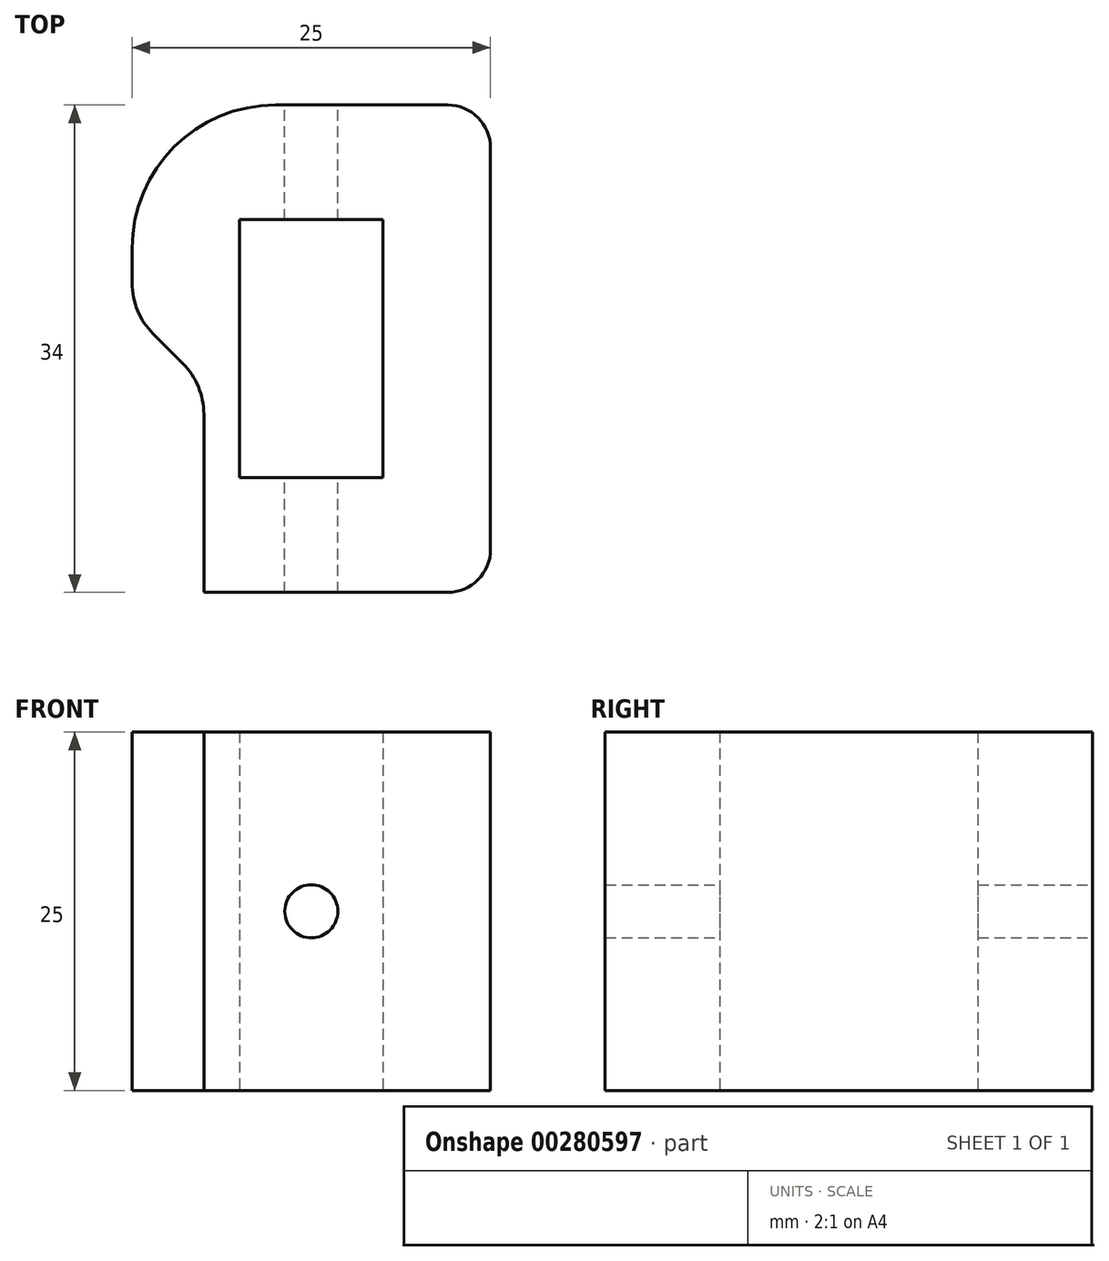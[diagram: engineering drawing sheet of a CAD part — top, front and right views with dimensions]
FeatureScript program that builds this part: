
annotation { "Feature Type Name" : "Feature", "Feature Type Description" : "" }
export const myFeature = defineFeature(function(context is Context, id is Id, definition is map)
    precondition{}
    {
        {
            var Q0;
            Q0=qCreatedBy(makeId("Top.planeOp"),FACE);
            var sketch = newSketch(context, id + "F0", { "sketchPlane" : qUnion([Q0])});
            skLineSegment(sketch, "E0", {"start": v(0, 0) * mm, "end": v(7.5, 0) * mm});
            skLineSegment(sketch, "E1", {"start": v(12.5, 34) * mm, "end": v(12.5, 19.5) * mm});
            skLineSegment(sketch, "E2", {"start": v(12.5, 34) * mm, "end": v(0, 34) * mm});
            skLineSegment(sketch, "E3.MirrorCS", {"start": v(-7.5, 14.5) * mm, "end": v(-12.5, 14.5) * mm, "construction": true});
            skLineSegment(sketch, "E4.MirrorCS", {"start": v(-12.5, 14.5) * mm, "end": v(-12.5, 19.5) * mm, "construction": true});
            skLineSegment(sketch, "E5.MirrorCS", {"start": v(-12.5, 34) * mm, "end": v(-12.5, 19.5) * mm});
            skLineSegment(sketch, "E6.MirrorCS", {"start": v(0, 0) * mm, "end": v(-7.5, 0) * mm});
            skLineSegment(sketch, "E7.MirrorCS", {"start": v(-7.5, 0) * mm, "end": v(-7.5, 14.5) * mm});
            skLineSegment(sketch, "E8.MirrorCS", {"start": v(-12.5, 34) * mm, "end": v(0, 34) * mm});
            skLineSegment(sketch, "E9.MirrorCS", {"start": v(-7.5, 14.5) * mm, "end": v(-12.5, 19.5) * mm});
            skLineSegment(sketch, "E10.0", {"start": v(-10, 21.5) * mm, "end": v(-10, 20.54) * mm});
            skLineSegment(sketch, "E10.2", {"start": v(0, 31.5) * mm, "end": v(0, 31.5) * mm});
            skLineSegment(sketch, "E10.3", {"start": v(-5, 8) * mm, "end": v(-5, 26) * mm});
            skLineSegment(sketch, "E10.6", {"start": v(0, 31.5) * mm, "end": v(0, 31.5) * mm});
            skLineSegment(sketch, "E10.7", {"start": v(10, 21.5) * mm, "end": v(10, 20.54) * mm});
            skLineSegment(sketch, "E10.9", {"start": v(5, 8) * mm, "end": v(5, 26) * mm});
            skLineSegment(sketch, "E11", {"start": v(-5, 8) * mm, "end": v(5, 8) * mm});
            skPoint(sketch, "E12.orphan", {"position": v(-5, -10) * mm});
            skPoint(sketch, "E13.orphan", {"position": v(5, -10) * mm});
            skPoint(sketch, "E14.visualSharp", {"position": v(-10, 31.5) * mm});
            skPoint(sketch, "E15.visualSharp", {"position": v(10, 31.5) * mm});
            skLineSegment(sketch, "E16", {"start": v(12.5, 19.5) * mm, "end": v(12.5, 0) * mm});
            skLineSegment(sketch, "E17", {"start": v(12.5, 0) * mm, "end": v(7.5, 0) * mm});
            skLineSegment(sketch, "E18", {"start": v(-5, 26) * mm, "end": v(5, 26) * mm});
            skSolve(sketch);
        }
        {
            var Q0;
            Q0=makeQuery(id+"F0.imprint","IMPRINT",FACE,{"disambiguationData":[TD([[makeQuery(id+"F0.imprint","IMPRINT",EDGE,{"derivedFrom":sQuery(id+"F0.wireOp",EDGE,"E0")}),1.0]])]});
            extrude(context, id + "F1", {"entities" : qUnion([Q0]), "depth" : 25 * mm});
        }
        {
            var Q0;
            Q0=makeQuery(id+"F1.opExtrude","SWEPT_EDGE",EDGE,{"disambiguationData":[OSD([sQuery(id+"F0.wireOp",EDGE,"E5.MirrorCS"),sQuery(id+"F0.wireOp",EDGE,"E9.MirrorCS")])]});
            var Q1;
            Q1=makeQuery(id+"F1.opExtrude","SWEPT_EDGE",EDGE,{"disambiguationData":[OSD([sQuery(id+"F0.wireOp",EDGE,"E7.MirrorCS"),sQuery(id+"F0.wireOp",EDGE,"E9.MirrorCS")])]});
            fillet(context, id + "F2", {"entities" : qUnion([Q0, Q1]), "radius" : 5 * mm, "tangentPropagation" : true, "allowEdgeOverflow" : false});
        }
        {
            var Q0;
            Q0=makeQuery(id+"F1.opExtrude","SWEPT_FACE",FACE,{"disambiguationData":[OSD([sQuery(id+"F0.wireOp",EDGE,"E11")])]});
            var sketch = newSketch(context, id + "F3", { "sketchPlane" : qUnion([Q0])});
            skLineSegment(sketch, "E19", {"start": v(-5, 25) * mm, "end": v(5, 0) * mm, "construction": true});
            skLineSegment(sketch, "E20", {"start": v(-5, 0) * mm, "end": v(5, 25) * mm, "construction": true});
            skCircle(sketch, "E21", {"center": v(0, 12.5) * mm, "radius": 1.85 * mm});
            skSolve(sketch);
        }
        {
            var Q0;
            Q0=qSketchRegion(id+"F3",true);
            extrude(context, id + "F4", {"entities" : qUnion([Q0]), "operationType" : NewBodyOperationType.REMOVE, "endBound" : BoundingType.SYMMETRIC, "oppositeDirection" : true, "depth" : 100 * mm});
        }
        {
            var Q0;
            Q0=makeQuery(id+"F1.opExtrude","SWEPT_EDGE",EDGE,{"disambiguationData":[OSD([sQuery(id+"F0.wireOp",EDGE,"E5.MirrorCS"),sQuery(id+"F0.wireOp",EDGE,"E8.MirrorCS")])]});
            fillet(context, id + "F5", {"entities" : qUnion([Q0]), "radius" : 10 * mm, "tangentPropagation" : true, "allowEdgeOverflow" : false});
        }
        {
            var Q0;
            Q0=makeQuery(id+"F1.opExtrude","SWEPT_EDGE",EDGE,{"disambiguationData":[OSD([sQuery(id+"F0.wireOp",EDGE,"E1"),sQuery(id+"F0.wireOp",EDGE,"E2")])]});
            var Q1;
            Q1=makeQuery(id+"F1.opExtrude","SWEPT_EDGE",EDGE,{"disambiguationData":[OSD([sQuery(id+"F0.wireOp",EDGE,"E16"),sQuery(id+"F0.wireOp",EDGE,"E17")])]});
            fillet(context, id + "F6", {"entities" : qUnion([Q0, Q1]), "radius" : 3 * mm, "tangentPropagation" : true, "allowEdgeOverflow" : false});
        }
    });
